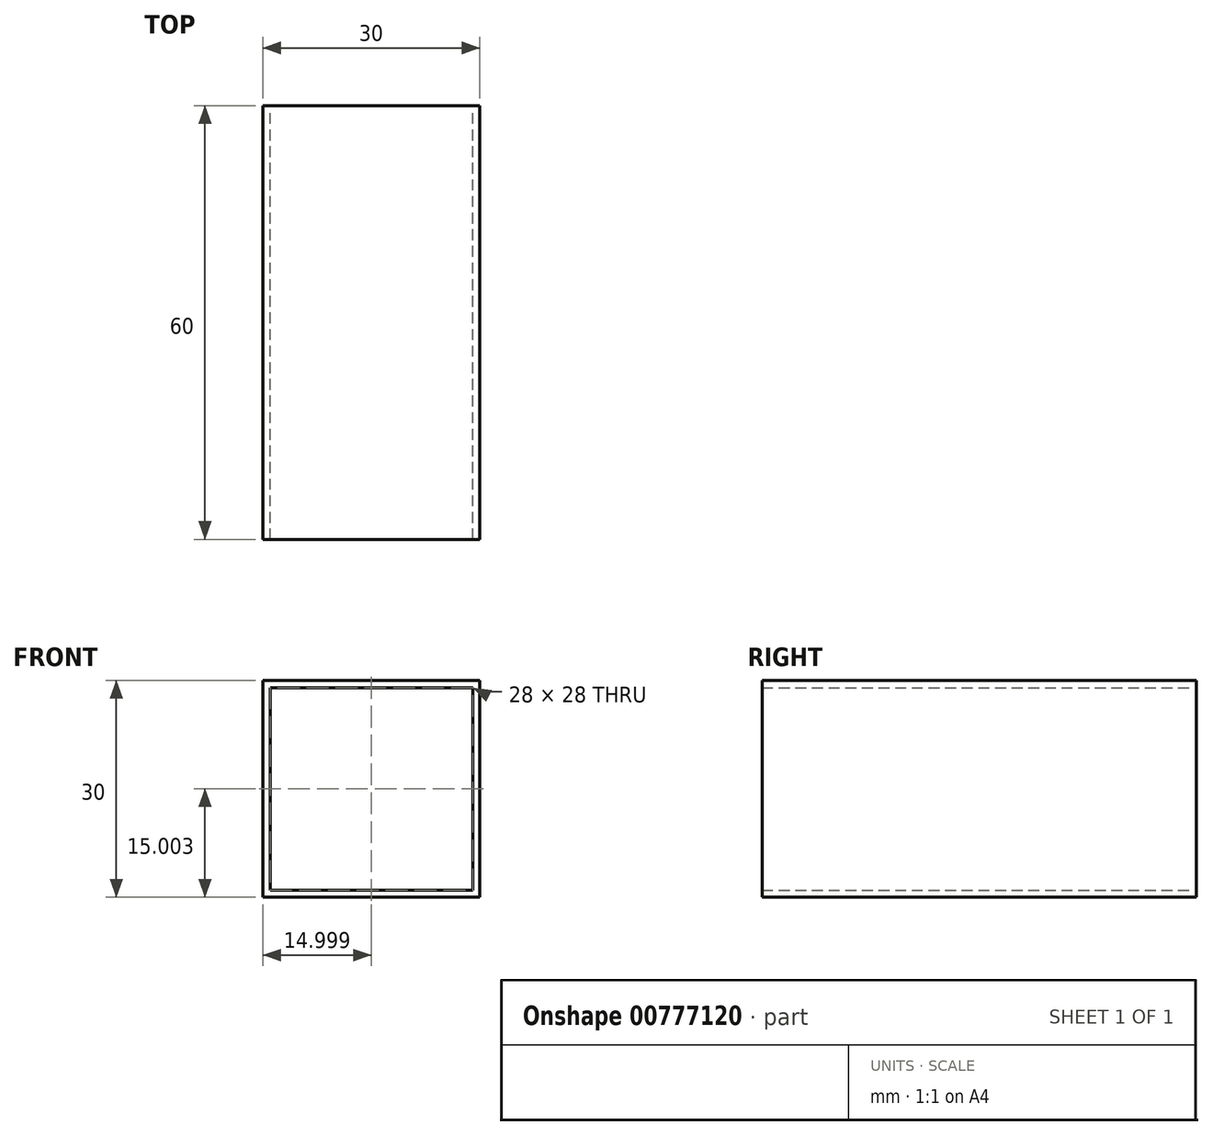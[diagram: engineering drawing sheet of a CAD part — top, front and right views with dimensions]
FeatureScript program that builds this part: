
annotation { "Feature Type Name" : "Feature", "Feature Type Description" : "" }
export const myFeature = defineFeature(function(context is Context, id is Id, definition is map)
    precondition{}
    {
        {
            var Q0;
            Q0=qCreatedBy(makeId("Front.planeOp"),FACE);
            var sketch = newSketch(context, id + "F0", { "sketchPlane" : qUnion([Q0])});
            skLineSegment(sketch, "E0.bottom", {"start": v(-69.81, 47.21) * mm, "end": v(-39.81, 47.21) * mm});
            skLineSegment(sketch, "E0.top", {"start": v(-69.81, 17.21) * mm, "end": v(-39.81, 17.21) * mm});
            skLineSegment(sketch, "E0.left", {"start": v(-69.81, 47.21) * mm, "end": v(-69.81, 17.21) * mm});
            skLineSegment(sketch, "E0.right", {"start": v(-39.81, 47.21) * mm, "end": v(-39.81, 17.21) * mm});
            skLineSegment(sketch, "E1.bottom", {"start": v(-68.81, 46.21) * mm, "end": v(-40.81, 46.21) * mm});
            skLineSegment(sketch, "E1.top", {"start": v(-68.81, 18.21) * mm, "end": v(-40.81, 18.21) * mm});
            skLineSegment(sketch, "E1.left", {"start": v(-68.81, 46.21) * mm, "end": v(-68.81, 18.21) * mm});
            skLineSegment(sketch, "E1.right", {"start": v(-40.81, 46.21) * mm, "end": v(-40.81, 18.21) * mm});
            skSolve(sketch);
        }
        {
            var Q0;
            Q0=makeQuery(id+"F0.imprint","IMPRINT",FACE,{"disambiguationData":[TD([[makeQuery(id+"F0.imprint","IMPRINT",EDGE,{"derivedFrom":sQuery(id+"F0.wireOp",EDGE,"E0.bottom")}),-1.0]])]});
            extrude(context, id + "F1", {"entities" : qUnion([Q0]), "depth" : 60 * mm, "offsetDistance" : 25 * mm});
        }
    });
